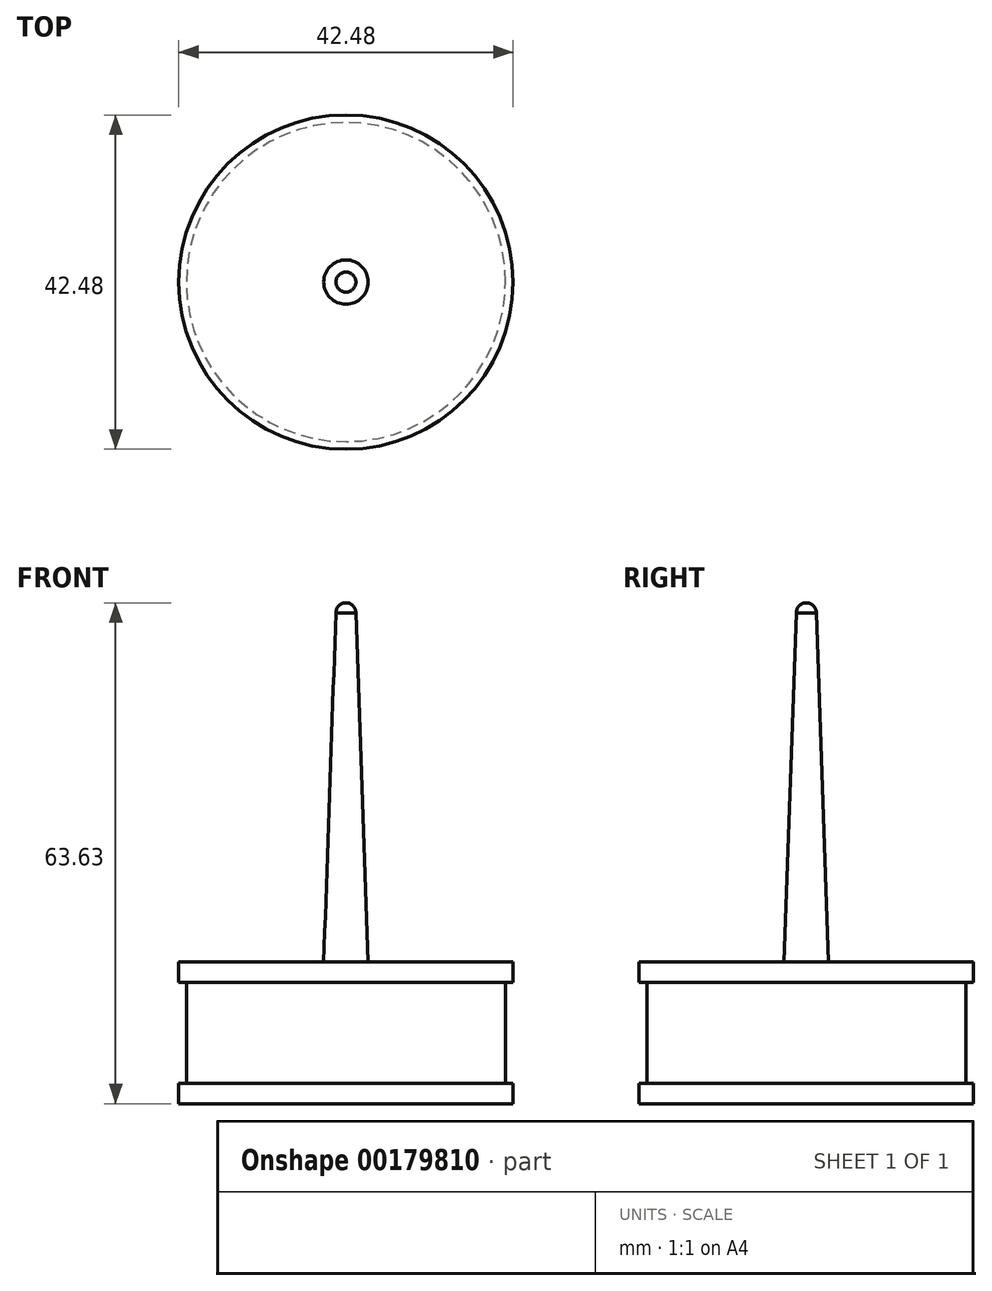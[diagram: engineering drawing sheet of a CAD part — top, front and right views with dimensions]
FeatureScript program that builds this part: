
annotation { "Feature Type Name" : "Feature", "Feature Type Description" : "" }
export const myFeature = defineFeature(function(context is Context, id is Id, definition is map)
    precondition{}
    {
        {
            var Q0;
            Q0=qCreatedBy(makeId("Right.planeOp"),FACE);
            var sketch = newSketch(context, id + "F0", { "sketchPlane" : qUnion([Q0])});
            skLineSegment(sketch, "E0", {"start": v(-21.24, 0) * mm, "end": v(0, 0) * mm});
            skLineSegment(sketch, "E1", {"start": v(0, 0) * mm, "end": v(0, -17.99) * mm});
            skLineSegment(sketch, "E2", {"start": v(0, -17.99) * mm, "end": v(-21.24, -17.99) * mm});
            skLineSegment(sketch, "E3", {"start": v(-21.24, -17.99) * mm, "end": v(-21.24, -15.42) * mm});
            skLineSegment(sketch, "E4", {"start": v(-21.24, -15.42) * mm, "end": v(-20.27, -15.42) * mm});
            skLineSegment(sketch, "E5", {"start": v(-20.27, -15.42) * mm, "end": v(-20.27, -2.57) * mm});
            skLineSegment(sketch, "E6", {"start": v(-20.27, -2.57) * mm, "end": v(-21.24, -2.57) * mm});
            skLineSegment(sketch, "E7", {"start": v(-21.24, -2.57) * mm, "end": v(-21.24, 0) * mm});
            skSolve(sketch);
        }
        {
            var Q0;
            Q0=qCreatedBy(makeId("Right.planeOp"),FACE);
            var sketch = newSketch(context, id + "F1", { "sketchPlane" : qUnion([Q0])});
            skLineSegment(sketch, "E8", {"start": v(0, -21.18) * mm, "end": v(0, 9.2) * mm, "construction": true});
            skSolve(sketch);
        }
        {
            var Q0;
            Q0 = qSketchRegion(id + "F0", true);
            var Q1;
            Q1=sQuery(id+"F1.wireOp",EDGE,"E8");
            revolve(context, id + "F2", {"entities" : qUnion([Q0]), "axis" : qUnion([Q1]), "revolveType" : RevolveType.FULL});
        }
        {
            var Q0;
            Q0=qCreatedBy(makeId("Right.planeOp"),FACE);
            var sketch = newSketch(context, id + "F3", { "sketchPlane" : qUnion([Q0])});
            skLineSegment(sketch, "E9", {"start": v(0, 0) * mm, "end": v(2.82, 0) * mm});
            skLineSegment(sketch, "E10", {"start": v(0, 44.37) * mm, "end": v(0, 0) * mm});
            skLineSegment(sketch, "E11", {"start": v(0, 44.37) * mm, "end": v(1.27, 44.37) * mm});
            skLineSegment(sketch, "E12", {"start": v(1.27, 44.37) * mm, "end": v(2.82, 0) * mm});
            skArc(sketch, "E13", {"start": v(1.27, 44.37) * mm, "mid": v(0.9, 45.27) * mm, "end": v(0, 45.64) * mm});
            skLineSegment(sketch, "E14", {"start": v(0, 45.64) * mm, "end": v(0, 44.37) * mm});
            skSolve(sketch);
        }
        {
            var Q0;
            Q0 = qSketchRegion(id + "F3", true);
            var Q1;
            Q1=sQuery(id+"F1.wireOp",EDGE,"E8");
            revolve(context, id + "F4", {"entities" : qUnion([Q0]), "axis" : qUnion([Q1]), "revolveType" : RevolveType.FULL});
        }
    });
